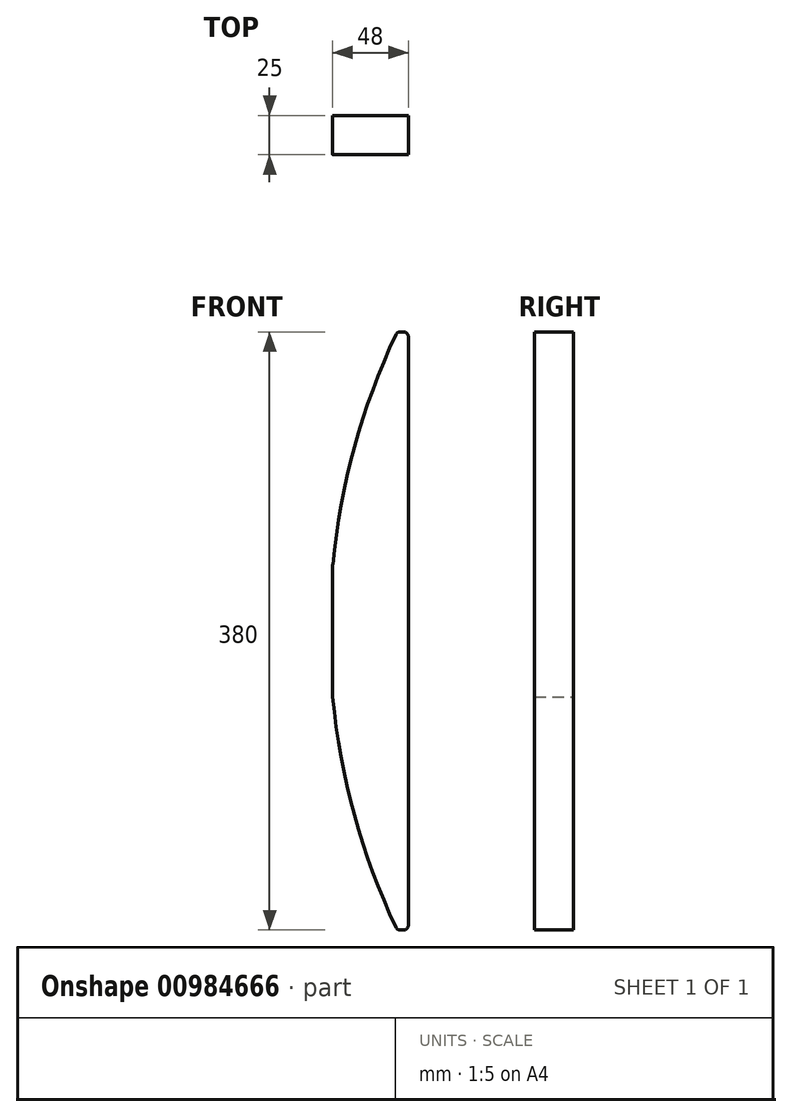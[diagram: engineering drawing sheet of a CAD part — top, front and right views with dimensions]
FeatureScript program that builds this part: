
annotation { "Feature Type Name" : "Feature", "Feature Type Description" : "" }
export const myFeature = defineFeature(function(context is Context, id is Id, definition is map)
    precondition{}
    {
        {
            var Q0;
            Q0=qCreatedBy(makeId("Front.planeOp"),FACE);
            var sketch = newSketch(context, id + "F0", { "sketchPlane" : qUnion([Q0])});
            skLineSegment(sketch, "E0", {"start": v(0, 0) * mm, "end": v(0, 380) * mm});
            skLineSegment(sketch, "E1", {"start": v(0, 190) * mm, "end": v(-50, 190) * mm, "construction": true});
            skLineSegment(sketch, "E2", {"start": v(0, 380) * mm, "end": v(-7, 380) * mm});
            skLineSegment(sketch, "E3.MirrorCS", {"start": v(0, 0) * mm, "end": v(-7, 0) * mm});
            skArc(sketch, "E4", {"start": v(-7, 380) * mm, "mid": v(-34, 307.78) * mm, "end": v(-48, 231.97) * mm});
            skLineSegment(sketch, "E5", {"start": v(-50, 190) * mm, "end": v(-48, 190) * mm, "construction": true});
            skLineSegment(sketch, "E6", {"start": v(-48, 190) * mm, "end": v(-48, 318.52) * mm});
            skLineSegment(sketch, "E7", {"start": v(-48, 318.52) * mm, "end": v(-108.44, 318.52) * mm});
            skLineSegment(sketch, "E8", {"start": v(-108.44, 318.52) * mm, "end": v(-108.44, 90.04) * mm});
            skLineSegment(sketch, "E9", {"start": v(-48, 190) * mm, "end": v(-48, 62.58) * mm});
            skArc(sketch, "E10.trimOffspring", {"start": v(-48, 148.03) * mm, "mid": v(-34, 72.22) * mm, "end": v(-7, 0) * mm});
            skSolve(sketch);
        }
        {
            var Q0;
            Q0 = qSketchRegion(id + "F0", true);
            extrude(context, id + "F1", {"entities" : qUnion([Q0]), "depth" : 25 * mm, "offsetDistance" : 25 * mm});
        }
        {
            var Q0;
            Q0=makeQuery(id+"F1.opExtrude","SWEPT_EDGE",EDGE,{"disambiguationData":[OSD([sQuery(id+"F0.wireOp",EDGE,"E2"),sQuery(id+"F0.wireOp",EDGE,"E4")])]});
            var Q1;
            Q1=makeQuery(id+"F1.opExtrude","SWEPT_EDGE",EDGE,{"disambiguationData":[OSD([sQuery(id+"F0.wireOp",EDGE,"E0"),sQuery(id+"F0.wireOp",EDGE,"E2")])]});
            var Q2;
            Q2=makeQuery(id+"F1.opExtrude","SWEPT_EDGE",EDGE,{"disambiguationData":[OSD([sQuery(id+"F0.wireOp",EDGE,"E0"),sQuery(id+"F0.wireOp",EDGE,"E3.MirrorCS")])]});
            var Q3;
            Q3=makeQuery(id+"F1.opExtrude","SWEPT_EDGE",EDGE,{"disambiguationData":[OSD([sQuery(id+"F0.wireOp",EDGE,"E3.MirrorCS"),sQuery(id+"F0.wireOp",EDGE,"E4")])]});
            fillet(context, id + "F2", {"entities" : qUnion([Q0, Q1, Q2, Q3]), "radius" : 3 * mm, "tangentPropagation" : true, "allowEdgeOverflow" : false});
        }
    });
